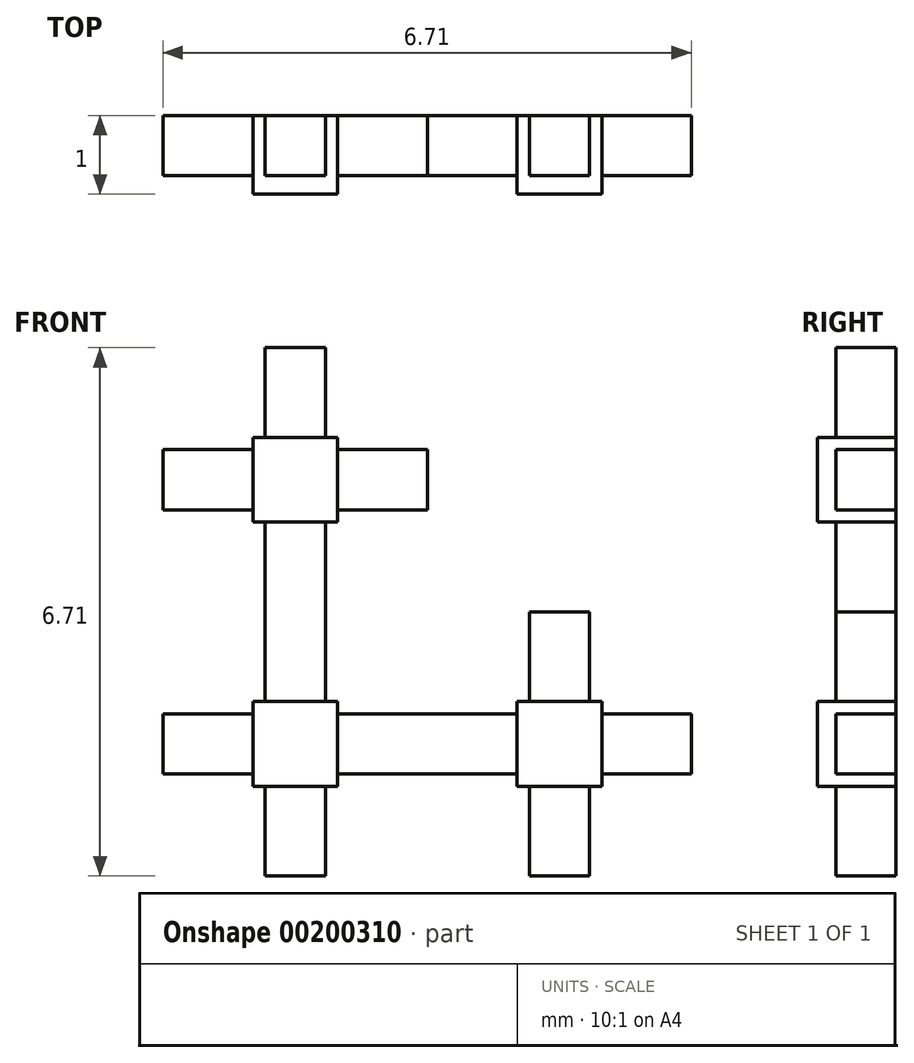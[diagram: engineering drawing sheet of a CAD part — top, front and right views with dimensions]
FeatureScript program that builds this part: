
annotation { "Feature Type Name" : "Feature", "Feature Type Description" : "" }
export const myFeature = defineFeature(function(context is Context, id is Id, definition is map)
    precondition{}
    {
        {
            var Q0;
            Q0=qCreatedBy(makeId("Front.planeOp"),FACE);
            var sketch = newSketch(context, id + "F0", { "sketchPlane" : qUnion([Q0])});
            skLineSegment(sketch, "E0.bottom", {"start": v(0.54, 0.54) * mm, "end": v(-0.54, 0.54) * mm});
            skLineSegment(sketch, "E0.top", {"start": v(0.54, -0.54) * mm, "end": v(-0.54, -0.54) * mm});
            skLineSegment(sketch, "E0.left", {"start": v(0.54, 0.54) * mm, "end": v(0.54, -0.54) * mm});
            skLineSegment(sketch, "E0.right", {"start": v(-0.54, 0.54) * mm, "end": v(-0.54, -0.54) * mm});
            skPoint(sketch, "E0.middle", {"position": v(0, 0) * mm});
            skSolve(sketch);
        }
        {
            var Q0;
            Q0=qSketchRegion(id+"F0",true);
            extrude(context, id + "F1", {"entities" : qUnion([Q0]), "depth" : 1 * mm});
        }
        {
            var Q0;
            Q0=makeQuery(id+"F1.opExtrude","SWEPT_FACE",FACE,{"disambiguationData":[OSD([sQuery(id+"F0.wireOp",EDGE,"E0.top")])]});
            var sketch = newSketch(context, id + "F2", { "sketchPlane" : qUnion([Q0])});
            skLineSegment(sketch, "E1", {"start": v(-0.54, 0) * mm, "end": v(-0.38, 0) * mm});
            skLineSegment(sketch, "E2", {"start": v(0.54, 0) * mm, "end": v(0.38, 0) * mm});
            skLineSegment(sketch, "E3.bottom", {"start": v(-0.38, 0) * mm, "end": v(0.38, 0) * mm});
            skLineSegment(sketch, "E3.top", {"start": v(-0.38, 0.76) * mm, "end": v(0.38, 0.76) * mm});
            skLineSegment(sketch, "E3.left", {"start": v(-0.38, 0) * mm, "end": v(-0.38, 0.76) * mm});
            skLineSegment(sketch, "E3.right", {"start": v(0.38, 0) * mm, "end": v(0.38, 0.76) * mm});
            skSolve(sketch);
        }
        {
            var Q0;
            Q0=qSketchRegion(id+"F2",true);
            extrude(context, id + "F3", {"entities" : qUnion([Q0]), "operationType" : NewBodyOperationType.ADD, "depth" : 1.14 * mm});
        }
        {
            var Q0;
            Q0=makeQuery(id+"F1.opExtrude","SWEPT_FACE",FACE,{"disambiguationData":[OSD([sQuery(id+"F0.wireOp",EDGE,"E0.right")])]});
            var sketch = newSketch(context, id + "F4", { "sketchPlane" : qUnion([Q0])});
            skLineSegment(sketch, "E4", {"start": v(0, -0.54) * mm, "end": v(0, -0.38) * mm});
            skLineSegment(sketch, "E5.bottom", {"start": v(0, -0.38) * mm, "end": v(0.76, -0.38) * mm});
            skLineSegment(sketch, "E5.top", {"start": v(0, 0.38) * mm, "end": v(0.76, 0.38) * mm});
            skLineSegment(sketch, "E5.left", {"start": v(0, -0.38) * mm, "end": v(0, 0.38) * mm});
            skLineSegment(sketch, "E5.right", {"start": v(0.76, -0.38) * mm, "end": v(0.76, 0.38) * mm});
            skSolve(sketch);
        }
        {
            var Q0;
            Q0=qSketchRegion(id+"F4",true);
            extrude(context, id + "F5", {"entities" : qUnion([Q0]), "operationType" : NewBodyOperationType.ADD, "depth" : 1.14 * mm});
        }
        {
            var Q0;
            Q0=makeQuery(id+"F1.opExtrude","SWEPT_FACE",FACE,{"disambiguationData":[OSD([sQuery(id+"F0.wireOp",EDGE,"E0.left")])]});
            var sketch = newSketch(context, id + "F6", { "sketchPlane" : qUnion([Q0])});
            skLineSegment(sketch, "E6", {"start": v(0, 0.54) * mm, "end": v(0, 0.38) * mm});
            skLineSegment(sketch, "E7.bottom", {"start": v(0, 0.38) * mm, "end": v(-0.76, 0.38) * mm});
            skLineSegment(sketch, "E7.top", {"start": v(0, -0.38) * mm, "end": v(-0.76, -0.38) * mm});
            skLineSegment(sketch, "E7.left", {"start": v(0, 0.38) * mm, "end": v(0, -0.38) * mm});
            skLineSegment(sketch, "E7.right", {"start": v(-0.76, 0.38) * mm, "end": v(-0.76, -0.38) * mm});
            skSolve(sketch);
        }
        {
            var Q0;
            Q0=qSketchRegion(id+"F6",true);
            extrude(context, id + "F7", {"entities" : qUnion([Q0]), "operationType" : NewBodyOperationType.ADD, "depth" : 1.14 * mm});
        }
        {
            var Q0;
            Q0=makeQuery(id+"F1.opExtrude","SWEPT_FACE",FACE,{"disambiguationData":[OSD([sQuery(id+"F0.wireOp",EDGE,"E0.bottom")])]});
            var sketch = newSketch(context, id + "F8", { "sketchPlane" : qUnion([Q0])});
            skLineSegment(sketch, "E8", {"start": v(0.54, 0) * mm, "end": v(0.38, 0) * mm});
            skLineSegment(sketch, "E9.bottom", {"start": v(0.38, 0) * mm, "end": v(-0.38, 0) * mm});
            skLineSegment(sketch, "E9.top", {"start": v(0.38, -0.76) * mm, "end": v(-0.38, -0.76) * mm});
            skLineSegment(sketch, "E9.left", {"start": v(0.38, 0) * mm, "end": v(0.38, -0.76) * mm});
            skLineSegment(sketch, "E9.right", {"start": v(-0.38, 0) * mm, "end": v(-0.38, -0.76) * mm});
            skSolve(sketch);
        }
        {
            var Q0;
            Q0=qSketchRegion(id+"F8",true);
            extrude(context, id + "F9", {"entities" : qUnion([Q0]), "operationType" : NewBodyOperationType.ADD, "depth" : 2.27 * mm});
        }
        {
            var Q0;
            Q0=makeQuery(id+"F9.opExtrude","CAP_FACE",FACE,{"disambiguationData":[OSD([sQuery(id+"F8.wireOp",EDGE,"E9.bottom"),sQuery(id+"F8.wireOp",EDGE,"E9.top"),sQuery(id+"F8.wireOp",EDGE,"E9.left"),sQuery(id+"F8.wireOp",EDGE,"E9.right")])],"isStart":false});
            var sketch = newSketch(context, id + "F10", { "sketchPlane" : qUnion([Q0])});
            skLineSegment(sketch, "E10", {"start": v(0.38, 0) * mm, "end": v(0.54, 0) * mm});
            skLineSegment(sketch, "E11.bottom", {"start": v(0.54, 0) * mm, "end": v(-0.54, 0) * mm});
            skLineSegment(sketch, "E11.top", {"start": v(0.54, -1) * mm, "end": v(-0.54, -1) * mm});
            skLineSegment(sketch, "E11.left", {"start": v(0.54, 0) * mm, "end": v(0.54, -1) * mm});
            skLineSegment(sketch, "E11.right", {"start": v(-0.54, 0) * mm, "end": v(-0.54, -1) * mm});
            skSolve(sketch);
        }
        {
            var Q0;
            Q0=qSketchRegion(id+"F10",true);
            extrude(context, id + "F11", {"entities" : qUnion([Q0]), "operationType" : NewBodyOperationType.ADD, "depth" : 1.08 * mm});
        }
        {
            var Q0;
            Q0=makeQuery(id+"F11.opExtrude","SWEPT_FACE",FACE,{"disambiguationData":[OSD([sQuery(id+"F10.wireOp",EDGE,"E11.left")])]});
            var sketch = newSketch(context, id + "F12", { "sketchPlane" : qUnion([Q0])});
            skLineSegment(sketch, "E12", {"start": v(0, 2.81) * mm, "end": v(0, 2.97) * mm});
            skLineSegment(sketch, "E13.bottom", {"start": v(0, 2.97) * mm, "end": v(-0.76, 2.97) * mm});
            skLineSegment(sketch, "E13.top", {"start": v(0, 3.73) * mm, "end": v(-0.76, 3.73) * mm});
            skLineSegment(sketch, "E13.left", {"start": v(0, 2.97) * mm, "end": v(0, 3.73) * mm});
            skLineSegment(sketch, "E13.right", {"start": v(-0.76, 2.97) * mm, "end": v(-0.76, 3.73) * mm});
            skSolve(sketch);
        }
        {
            var Q0;
            Q0=qSketchRegion(id+"F12",true);
            extrude(context, id + "F13", {"entities" : qUnion([Q0]), "operationType" : NewBodyOperationType.ADD, "depth" : 1.14 * mm});
        }
        {
            var Q0;
            Q0=makeQuery(id+"F11.opExtrude","CAP_FACE",FACE,{"disambiguationData":[OSD([sQuery(id+"F10.wireOp",EDGE,"E11.bottom"),sQuery(id+"F10.wireOp",EDGE,"E11.top"),sQuery(id+"F10.wireOp",EDGE,"E11.left"),sQuery(id+"F10.wireOp",EDGE,"E11.right")])],"isStart":false});
            var sketch = newSketch(context, id + "F14", { "sketchPlane" : qUnion([Q0])});
            skLineSegment(sketch, "E14", {"start": v(0.54, 0) * mm, "end": v(0.38, 0) * mm});
            skLineSegment(sketch, "E15.bottom", {"start": v(0.38, 0) * mm, "end": v(-0.38, 0) * mm});
            skLineSegment(sketch, "E15.top", {"start": v(0.38, -0.76) * mm, "end": v(-0.38, -0.76) * mm});
            skLineSegment(sketch, "E15.left", {"start": v(0.38, 0) * mm, "end": v(0.38, -0.76) * mm});
            skLineSegment(sketch, "E15.right", {"start": v(-0.38, 0) * mm, "end": v(-0.38, -0.76) * mm});
            skSolve(sketch);
        }
        {
            var Q0;
            Q0=qSketchRegion(id+"F14",true);
            extrude(context, id + "F15", {"entities" : qUnion([Q0]), "operationType" : NewBodyOperationType.ADD, "depth" : 1.14 * mm});
        }
        {
            var Q0;
            Q0=makeQuery(id+"F11.opExtrude","SWEPT_FACE",FACE,{"disambiguationData":[OSD([sQuery(id+"F10.wireOp",EDGE,"E11.right")])]});
            var sketch = newSketch(context, id + "F16", { "sketchPlane" : qUnion([Q0])});
            skLineSegment(sketch, "E16", {"start": v(0, 3.9) * mm, "end": v(0, 3.73) * mm});
            skLineSegment(sketch, "E17.bottom", {"start": v(0, 3.73) * mm, "end": v(0.76, 3.73) * mm});
            skLineSegment(sketch, "E17.top", {"start": v(0, 2.97) * mm, "end": v(0.76, 2.97) * mm});
            skLineSegment(sketch, "E17.left", {"start": v(0, 3.73) * mm, "end": v(0, 2.97) * mm});
            skLineSegment(sketch, "E17.right", {"start": v(0.76, 3.73) * mm, "end": v(0.76, 2.97) * mm});
            skSolve(sketch);
        }
        {
            var Q0;
            Q0=qSketchRegion(id+"F16",true);
            extrude(context, id + "F17", {"entities" : qUnion([Q0]), "operationType" : NewBodyOperationType.ADD, "depth" : 1.14 * mm});
        }
        {
            var Q0;
            Q0=makeQuery(id+"F7.opExtrude","CAP_FACE",FACE,{"disambiguationData":[OSD([sQuery(id+"F6.wireOp",EDGE,"E7.bottom"),sQuery(id+"F6.wireOp",EDGE,"E7.top"),sQuery(id+"F6.wireOp",EDGE,"E7.left"),sQuery(id+"F6.wireOp",EDGE,"E7.right")])],"isStart":false});
            var sketch = newSketch(context, id + "F18", { "sketchPlane" : qUnion([Q0])});
            skLineSegment(sketch, "E18.bottom", {"start": v(-0.76, -0.38) * mm, "end": v(0, -0.38) * mm});
            skLineSegment(sketch, "E18.top", {"start": v(-0.76, 0.38) * mm, "end": v(0, 0.38) * mm});
            skLineSegment(sketch, "E18.left", {"start": v(-0.76, -0.38) * mm, "end": v(-0.76, 0.38) * mm});
            skLineSegment(sketch, "E18.right", {"start": v(0, -0.38) * mm, "end": v(0, 0.38) * mm});
            skSolve(sketch);
        }
        {
            var Q0;
            Q0 = qSketchRegion(id + "F18", true);
            extrude(context, id + "F19", {"entities" : qUnion([Q0]), "operationType" : NewBodyOperationType.ADD, "depth" : 1.14 * mm});
        }
        {
            var Q0;
            Q0=makeQuery(id+"F19.opExtrude","CAP_FACE",FACE,{"disambiguationData":[OSD([sQuery(id+"F18.wireOp",EDGE,"E18.bottom"),sQuery(id+"F18.wireOp",EDGE,"E18.top"),sQuery(id+"F18.wireOp",EDGE,"E18.left"),sQuery(id+"F18.wireOp",EDGE,"E18.right")])],"isStart":false});
            var sketch = newSketch(context, id + "F20", { "sketchPlane" : qUnion([Q0])});
            skLineSegment(sketch, "E19", {"start": v(0, -0.38) * mm, "end": v(0, -0.54) * mm});
            skLineSegment(sketch, "E20.bottom", {"start": v(0, -0.54) * mm, "end": v(-1, -0.54) * mm});
            skLineSegment(sketch, "E20.top", {"start": v(0, 0.54) * mm, "end": v(-1, 0.54) * mm});
            skLineSegment(sketch, "E20.left", {"start": v(0, -0.54) * mm, "end": v(0, 0.54) * mm});
            skLineSegment(sketch, "E20.right", {"start": v(-1, -0.54) * mm, "end": v(-1, 0.54) * mm});
            skSolve(sketch);
        }
        {
            var Q0;
            Q0 = qSketchRegion(id + "F20", true);
            extrude(context, id + "F21", {"entities" : qUnion([Q0]), "operationType" : NewBodyOperationType.ADD, "depth" : 1.08 * mm});
        }
        {
            var Q0;
            Q0=makeQuery(id+"F21.opExtrude","SWEPT_FACE",FACE,{"disambiguationData":[OSD([sQuery(id+"F20.wireOp",EDGE,"E20.bottom")])]});
            var sketch = newSketch(context, id + "F22", { "sketchPlane" : qUnion([Q0])});
            skLineSegment(sketch, "E21", {"start": v(2.81, 0) * mm, "end": v(2.97, 0) * mm});
            skLineSegment(sketch, "E22.bottom", {"start": v(2.97, 0) * mm, "end": v(3.73, 0) * mm});
            skLineSegment(sketch, "E22.top", {"start": v(2.97, 0.76) * mm, "end": v(3.73, 0.76) * mm});
            skLineSegment(sketch, "E22.left", {"start": v(2.97, 0) * mm, "end": v(2.97, 0.76) * mm});
            skLineSegment(sketch, "E22.right", {"start": v(3.73, 0) * mm, "end": v(3.73, 0.76) * mm});
            skSolve(sketch);
        }
        {
            var Q0;
            Q0 = qSketchRegion(id + "F22", true);
            extrude(context, id + "F23", {"entities" : qUnion([Q0]), "operationType" : NewBodyOperationType.ADD, "depth" : 1.14 * mm});
        }
        {
            var Q0;
            Q0=makeQuery(id+"F21.opExtrude","CAP_FACE",FACE,{"disambiguationData":[OSD([sQuery(id+"F20.wireOp",EDGE,"E20.bottom"),sQuery(id+"F20.wireOp",EDGE,"E20.top"),sQuery(id+"F20.wireOp",EDGE,"E20.left"),sQuery(id+"F20.wireOp",EDGE,"E20.right")])],"isStart":false});
            var sketch = newSketch(context, id + "F24", { "sketchPlane" : qUnion([Q0])});
            skLineSegment(sketch, "E23", {"start": v(0, -0.54) * mm, "end": v(0, -0.38) * mm});
            skLineSegment(sketch, "E24.bottom", {"start": v(0, -0.38) * mm, "end": v(-0.76, -0.38) * mm});
            skLineSegment(sketch, "E24.top", {"start": v(0, 0.38) * mm, "end": v(-0.76, 0.38) * mm});
            skLineSegment(sketch, "E24.left", {"start": v(0, -0.38) * mm, "end": v(0, 0.38) * mm});
            skLineSegment(sketch, "E24.right", {"start": v(-0.76, -0.38) * mm, "end": v(-0.76, 0.38) * mm});
            skSolve(sketch);
        }
        {
            var Q0;
            Q0 = qSketchRegion(id + "F24", true);
            extrude(context, id + "F25", {"entities" : qUnion([Q0]), "operationType" : NewBodyOperationType.ADD, "depth" : 1.14 * mm});
        }
        {
            var Q0;
            Q0=makeQuery(id+"F21.opExtrude","SWEPT_FACE",FACE,{"disambiguationData":[OSD([sQuery(id+"F20.wireOp",EDGE,"E20.top")])]});
            var sketch = newSketch(context, id + "F26", { "sketchPlane" : qUnion([Q0])});
            skLineSegment(sketch, "E25", {"start": v(3.9, 0) * mm, "end": v(3.73, 0) * mm});
            skLineSegment(sketch, "E26.bottom", {"start": v(3.73, 0) * mm, "end": v(2.97, 0) * mm});
            skLineSegment(sketch, "E26.top", {"start": v(3.73, -0.76) * mm, "end": v(2.97, -0.76) * mm});
            skLineSegment(sketch, "E26.left", {"start": v(3.73, 0) * mm, "end": v(3.73, -0.76) * mm});
            skLineSegment(sketch, "E26.right", {"start": v(2.97, 0) * mm, "end": v(2.97, -0.76) * mm});
            skSolve(sketch);
        }
        {
            var Q0;
            Q0 = qSketchRegion(id + "F26", true);
            extrude(context, id + "F27", {"entities" : qUnion([Q0]), "operationType" : NewBodyOperationType.ADD, "depth" : 1.14 * mm});
        }
    });
